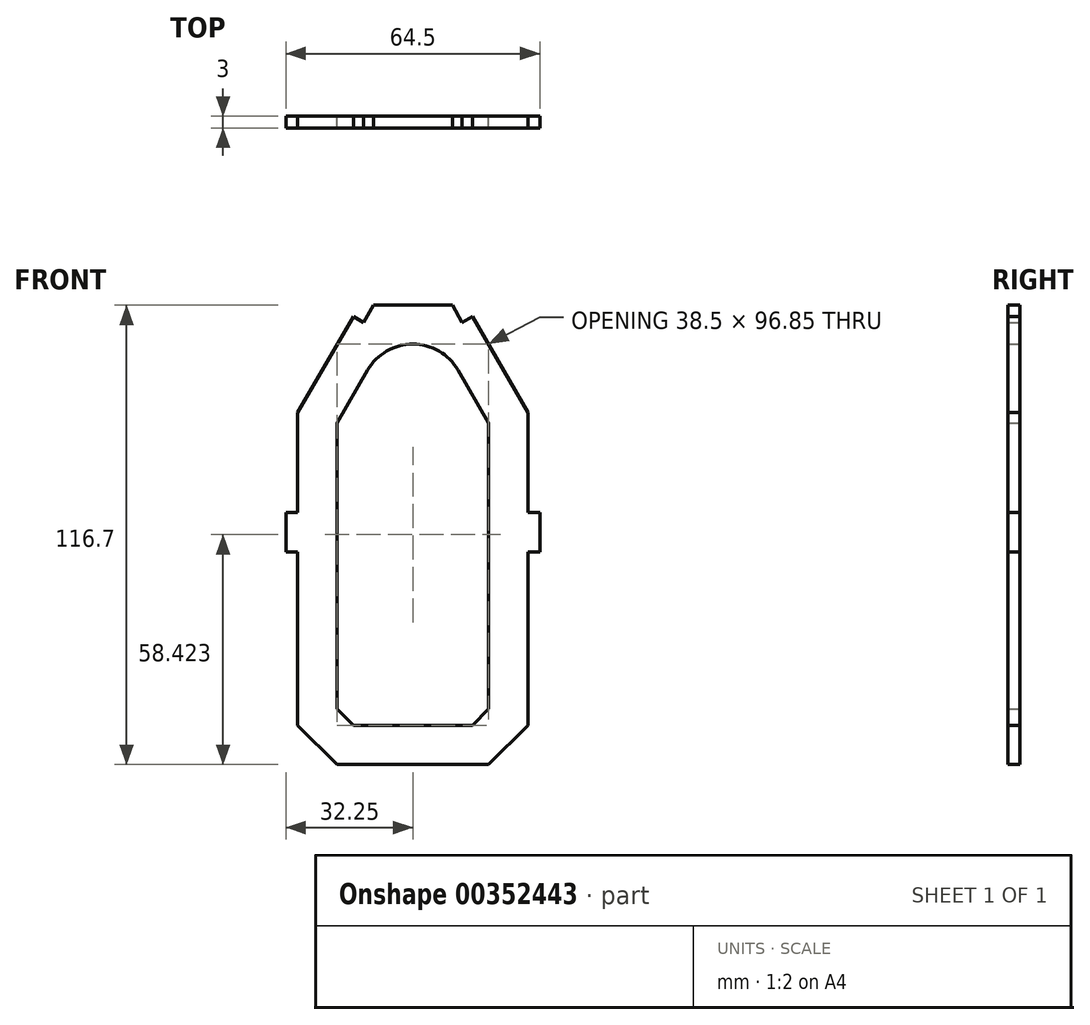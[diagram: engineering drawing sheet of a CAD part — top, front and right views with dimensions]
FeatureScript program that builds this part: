
annotation { "Feature Type Name" : "Feature", "Feature Type Description" : "" }
export const myFeature = defineFeature(function(context is Context, id is Id, definition is map)
    precondition{}
    {
        {
            var Q0;
            Q0=qCreatedBy(makeId("Front.planeOp"),FACE);
            var sketch = newSketch(context, id + "F0", { "sketchPlane" : qUnion([Q0])});
            skLineSegment(sketch, "E0.bottom", {"start": v(19.25, -59) * mm, "end": v(-19.25, -59) * mm});
            skLineSegment(sketch, "E0.top", {"start": v(10.04, 57.7) * mm, "end": v(-10.04, 57.7) * mm});
            skLineSegment(sketch, "E0.left", {"start": v(29.25, -49) * mm, "end": v(29.25, -5) * mm});
            skLineSegment(sketch, "E0.right", {"start": v(-29.25, -49) * mm, "end": v(-29.25, -5) * mm});
            skPoint(sketch, "E0.middle", {"position": v(0, -0.93) * mm});
            skPoint(sketch, "E1", {"position": v(-13.5, 57.7) * mm});
            skLineSegment(sketch, "E2", {"start": v(-15.13, 54.87) * mm, "end": v(-29.25, 30.44) * mm});
            skLineSegment(sketch, "E3", {"start": v(-10.04, 57.7) * mm, "end": v(-12.54, 53.37) * mm});
            skLineSegment(sketch, "E4", {"start": v(-12.54, 53.37) * mm, "end": v(-15.13, 54.87) * mm});
            skPoint(sketch, "E5.orphan", {"position": v(-29.25, 57.7) * mm});
            skLineSegment(sketch, "E6.MirrorCS", {"start": v(10.04, 57.7) * mm, "end": v(12.54, 53.37) * mm});
            skLineSegment(sketch, "E7.MirrorCS", {"start": v(12.54, 53.37) * mm, "end": v(15.13, 54.87) * mm});
            skLineSegment(sketch, "E8.MirrorCS", {"start": v(15.13, 54.87) * mm, "end": v(29.25, 30.44) * mm});
            skPoint(sketch, "E9.orphan", {"position": v(29.25, 57.7) * mm});
            skLineSegment(sketch, "E10", {"start": v(-29.25, 5) * mm, "end": v(-32.25, 5) * mm});
            skLineSegment(sketch, "E11", {"start": v(-32.25, 5) * mm, "end": v(-32.25, -5) * mm});
            skLineSegment(sketch, "E12", {"start": v(-32.25, -5) * mm, "end": v(-29.25, -5) * mm});
            skLineSegment(sketch, "E13.trimOffspring", {"start": v(-29.25, 5) * mm, "end": v(-29.25, 30.44) * mm});
            skLineSegment(sketch, "E14.MirrorCS", {"start": v(29.25, 5) * mm, "end": v(32.25, 5) * mm});
            skLineSegment(sketch, "E15.MirrorCS", {"start": v(32.25, 5) * mm, "end": v(32.25, -5) * mm});
            skLineSegment(sketch, "E16.MirrorCS", {"start": v(32.25, -5) * mm, "end": v(29.25, -5) * mm});
            skLineSegment(sketch, "E17.trimOffspring", {"start": v(29.25, 5) * mm, "end": v(29.25, 30.44) * mm});
            skLineSegment(sketch, "E18", {"start": v(-29.25, -49) * mm, "end": v(-19.25, -59) * mm});
            skLineSegment(sketch, "E19.MirrorCS", {"start": v(29.25, -49) * mm, "end": v(19.25, -59) * mm});
            skLineSegment(sketch, "E20.0", {"start": v(19.25, -44.86) * mm, "end": v(15.1, -49) * mm});
            skLineSegment(sketch, "E20.1", {"start": v(19.25, -44.86) * mm, "end": v(19.25, 0) * mm});
            skLineSegment(sketch, "E20.2", {"start": v(19.25, 0) * mm, "end": v(19.25, 27.76) * mm});
            skLineSegment(sketch, "E20.3", {"start": v(-11.48, 41.21) * mm, "end": v(-19.25, 27.76) * mm});
            skLineSegment(sketch, "E20.4", {"start": v(-19.25, 0) * mm, "end": v(-19.25, 27.76) * mm});
            skLineSegment(sketch, "E20.5", {"start": v(-19.25, -44.86) * mm, "end": v(-19.25, 0) * mm});
            skLineSegment(sketch, "E20.6", {"start": v(-19.25, -44.86) * mm, "end": v(-15.1, -49) * mm});
            skLineSegment(sketch, "E20.10", {"start": v(15.1, -49) * mm, "end": v(-15.1, -49) * mm});
            skLineSegment(sketch, "E20.13", {"start": v(11.47, 41.23) * mm, "end": v(19.25, 27.76) * mm});
            skArc(sketch, "E21", {"start": v(11.47, 41.23) * mm, "mid": v(0, 47.85) * mm, "end": v(-11.48, 41.21) * mm});
            skSolve(sketch);
        }
        {
            var Q0;
            Q0 = qSketchRegion(id + "F0", true);
            extrude(context, id + "F1", {"entities" : qUnion([Q0]), "depth" : 3 * mm, "symmetric" : true});
        }
    });
